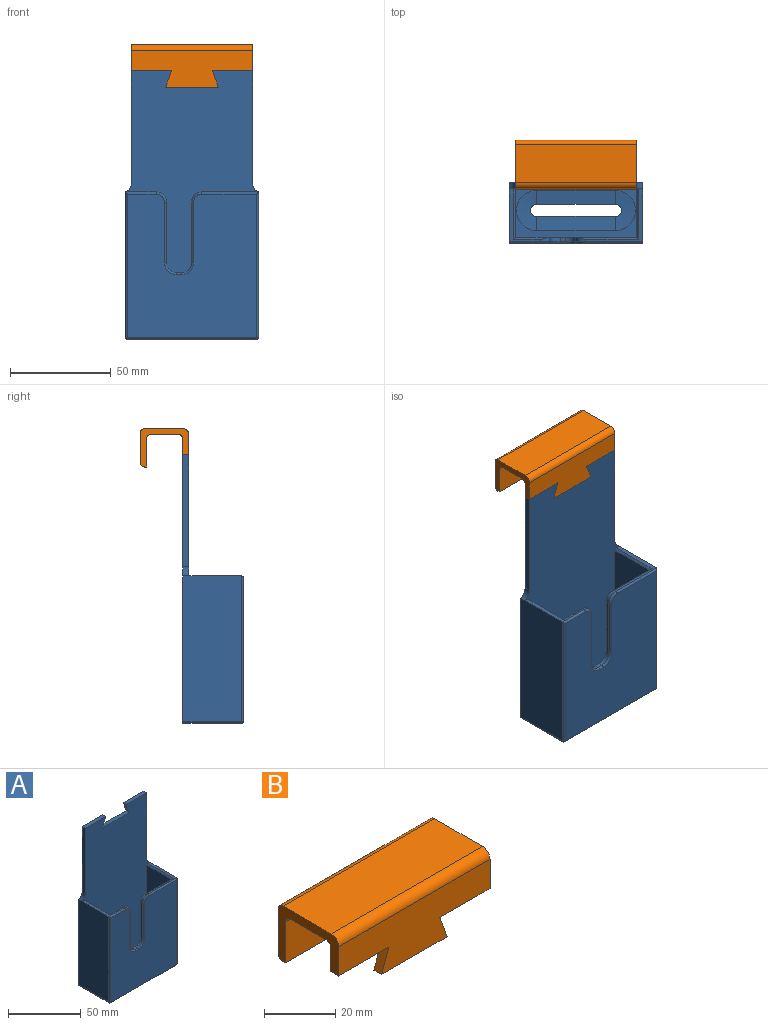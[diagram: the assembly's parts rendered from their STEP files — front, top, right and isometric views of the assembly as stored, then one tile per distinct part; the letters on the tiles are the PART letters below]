
ASSEMBLY  parts=2 mates=1
PART A: 56 faces, bbox 66x30x133 mm
  f0: plane 60x24mm, normal (0,0,1), area 345.8mm2, adj f1,f7,f16,f23,f24,f25,f26,f27
  f1: plane 69x24mm, normal (1,0,0), area 1656mm2, adj f0,f16,f17,f27
  f2: plane 26x15.27mm, normal (0,0,1), area 65.3mm2, adj f3,f16,f17,f34,f36,f45
  f3: plane 72x29mm, normal (-1,0,0), area 2088mm2, adj f2,f15,f47,f48,f54
  f4: plane 64x29mm, normal (0,0,-1), area 1593.7mm2, adj f15,f19,f20,f21,f22,f47,f50,f53
  f5: plane 72x29mm, normal (1,0,0), area 2088mm2, adj f6,f15,f49,f50,f55
  f6: plane 28.24x26mm, normal (0,0,1), area 78.2mm2, adj f5,f16,f18,f28,f37,f46
  f7: plane 69x24mm, normal (-1,0,0), area 1656mm2, adj f0,f16,f18,f27
  f8: plane 55.42x3mm, normal (-1,0,0), area 166.3mm2, adj f14,f15,f16,f54
  f9: plane 55.42x3mm, normal (1,0,0), area 166.3mm2, adj f10,f15,f16,f55
  f10: plane 19.91x3mm, normal (0,0,1), area 59.7mm2, adj f9,f11,f15,f16
  f11: plane 8x3mm, normal (-0.94,0,-0.34), area 25.5mm2, adj f10,f12,f15,f16
  f12: plane 26x3mm, normal (0,0,1), area 78mm2, adj f11,f13,f15,f16
  f13: plane 8x3mm, normal (0.94,0,-0.34), area 25.5mm2, adj f12,f14,f15,f16
  f14: plane 19.91x3mm, normal (0,0,1), area 59.7mm2, adj f8,f13,f15,f16
  f15: plane 133x66mm, normal (0,1,0), area 8240.5mm2, adj f3,f4,f5,f8,f9,f10,f11,f12
  f16: plane 130x66mm, normal (0,-1,0), area 7624mm2, adj f0,f1,f2,f6,f7,f8,f9,f10
  f17: plane 25x1mm, normal (0.71,0,0.71), area 34.6mm2, adj f1,f2,f16,f36
  f18: plane 25x1mm, normal (-0.71,0,0.71), area 34.6mm2, adj f6,f7,f16,f37
  f19: plane 39x2.39mm, normal (0,1,0), area 93.1mm2, adj f4,f20,f22,f24
  f20: cylinder r=3mm len=6mm, axis (0,0,-1), area 22.5mm2, adj f4,f19,f21,f23
  f21: plane 39x2.39mm, normal (0,-1,0), area 93.1mm2, adj f4,f20,f22,f25
  f22: cylinder r=3mm len=6mm, axis (0,0,-1), area 22.5mm2, adj f4,f19,f21,f26
  f23: cone r=3mm half-angle=85deg, axis (0,0,1), area 143.5mm2, adj f0,f20,f24,f25
  f24: plane 39x7mm, normal (0,0.09,1), area 274mm2, adj f0,f19,f23,f26
  f25: plane 39x7mm, normal (0,-0.09,1), area 274mm2, adj f0,f21,f23,f26
  f26: cone r=3mm half-angle=85deg, axis (0,0,1), area 143.5mm2, adj f0,f22,f24,f25
  f27: plane 69x60mm, normal (0,1,0), area 3658.9mm2, adj f0,f1,f7,f28,f29,f30,f31,f32
  f28: cylinder r=5mm len=5mm, axis (0,1,0), area 13.6mm2, adj f6,f27,f29,f37,f44
  f29: plane 30x2mm, normal (-1,0,0), area 60mm2, adj f27,f28,f30,f42
  f30: cylinder r=5mm len=5mm, axis (0,1,0), area 15.7mm2, adj f27,f29,f31,f40
  f31: plane 2.49x2mm, normal (0,0,1), area 5mm2, adj f27,f30,f32,f38
  f32: cylinder r=5mm len=5mm, axis (0,1,0), area 15.7mm2, adj f27,f31,f33,f39
  f33: plane 30x2mm, normal (1,0,0), area 60mm2, adj f27,f32,f34,f41
  f34: cylinder r=5mm len=5mm, axis (0,1,0), area 13.6mm2, adj f2,f27,f33,f36,f43
  f35: plane 71x64mm, normal (0,-1,0), area 3973.1mm2, adj f38,f39,f40,f41,f42,f43,f44,f45
  f36: plane 16.27x1mm, normal (0,0.71,0.71), area 20.9mm2, adj f2,f17,f27,f34
  f37: plane 29.24x1mm, normal (0,0.71,0.71), area 39.3mm2, adj f6,f18,f27,f28
  f38: cylinder r=1mm len=2.49mm, axis (1,0,0), area 3.9mm2, adj f31,f35,f39,f40
  f39: torus R=6mm, axis (0,-1,0), area 13.2mm2, adj f32,f35,f38,f41
  f40: torus R=6mm, axis (0,-1,0), area 13.2mm2, adj f30,f35,f38,f42
  f41: cylinder r=1mm len=30mm, axis (0,0,-1), area 47.1mm2, adj f33,f35,f39,f43
  f42: cylinder r=1mm len=30mm, axis (0,0,1), area 47.1mm2, adj f29,f35,f40,f44
  f43: torus R=4mm, axis (0,-1,0), area 11.4mm2, adj f34,f35,f41,f45
  f44: torus R=4mm, axis (0,-1,0), area 11.4mm2, adj f28,f35,f42,f46
  f45: cylinder r=1mm len=15.27mm, axis (1,0,0), area 23.4mm2, adj f2,f35,f43,f48
  f46: cylinder r=1mm len=28.24mm, axis (-1,0,0), area 43.8mm2, adj f6,f35,f44,f49
  f47: cylinder r=1mm len=29mm, axis (0,-1,0), area 45.6mm2, adj f3,f4,f15,f51
  f48: cylinder r=1mm len=72mm, axis (0,0,1), area 112.5mm2, adj f3,f35,f45,f51
  f49: cylinder r=1mm len=72mm, axis (0,0,-1), area 112.5mm2, adj f5,f35,f46,f52
  f50: cylinder r=1mm len=29mm, axis (0,1,0), area 45.6mm2, adj f4,f5,f15,f52
  f51: sphere r=1mm, area 1.6mm2, adj f47,f48,f53
  f52: sphere r=1mm, area 1.6mm2, adj f49,f50,f53
  f53: cylinder r=1mm len=64mm, axis (-1,0,0), area 100.5mm2, adj f4,f35,f51,f52
  f54: cylinder r=5mm len=4.58mm, axis (0,-1,0), area 17.4mm2, adj f3,f8,f15,f16
  f55: cylinder r=5mm len=4.58mm, axis (0,1,0), area 17.4mm2, adj f5,f9,f15,f16
PART B: 19 faces, bbox 60x24x21 mm
  f0: plane 60x14mm, normal (0,0,-1), area 840mm2, adj f1,f2,f16,f17
  f1: plane 24x19mm, normal (-1,0,0), area 148.1mm2, adj f0,f3,f4,f5,f6,f7,f12,f13
  f2: plane 24x19mm, normal (1,0,0), area 148.1mm2, adj f0,f3,f4,f5,f6,f11,f12,f13
  f3: plane 60x15mm, normal (0,1,0), area 900mm2, adj f1,f2,f5,f18
  f4: plane 60x19mm, normal (0,0,1), area 1140mm2, adj f1,f2,f5,f6
  f5: cylinder r=2mm len=60mm, axis (1,0,0), area 188.5mm2, adj f1,f2,f3,f4
  f6: cylinder r=3mm len=60mm, axis (-1,0,0), area 282.7mm2, adj f1,f2,f4,f12
  f7: plane 19.91x3mm, normal (0,0,-1), area 59.7mm2, adj f1,f8,f12,f13
  f8: plane 8x3mm, normal (-0.94,0,0.34), area 25.5mm2, adj f7,f9,f12,f13
  f9: plane 26x3mm, normal (0,0,-1), area 78mm2, adj f8,f10,f12,f13
  f10: plane 8x3mm, normal (0.94,0,0.34), area 25.5mm2, adj f9,f11,f12,f13
  f11: plane 19.91x3mm, normal (0,0,-1), area 59.7mm2, adj f2,f10,f12,f13
  f12: plane 60x18mm, normal (0,-1,0), area 784.7mm2, adj f1,f2,f6,f7,f8,f9,f10,f11
  f13: plane 60x16mm, normal (0,1,0), area 664.7mm2, adj f1,f2,f7,f8,f9,f10,f11,f16
  f14: plane 60x1mm, normal (0,0,-1), area 60mm2, adj f1,f2,f15,f18
  f15: plane 60x14mm, normal (0,-1,0), area 840mm2, adj f1,f2,f14,f17
  f16: cylinder r=2mm len=60mm, axis (-1,0,0), area 188.5mm2, adj f0,f1,f2,f13
  f17: cylinder r=2mm len=60mm, axis (-1,0,0), area 188.5mm2, adj f0,f1,f2,f15
  f18: cylinder r=2mm len=60mm, axis (1,0,0), area 188.5mm2, adj f1,f2,f3,f14
PLACE A t=(-24.78,13.98,-10.47)mm
PLACE B t=(2.75,25.98,81.74)mm
MATE fastened B.f12 <-> A.f16  axis (0,-1,0) through (2.75,13.98,63.74)mm
